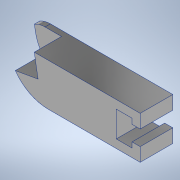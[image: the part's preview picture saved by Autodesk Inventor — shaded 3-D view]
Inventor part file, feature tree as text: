
AUTODESK INVENTOR PART (.ipt)
format: ipt  version: 2022 (Build 260153000, 153)  size: 164,352 bytes
history: native  units: mm
features: extrude x3, sketch x3, fillet x1
ambient origin geometry x8: Origin, YZ Plane, XZ Plane, XY Plane, X Axis, Y Axis, Z Axis, Center Point
bodies: Body1 (feature_tree)
feature tree (7):
  extrude  "Extrusion2"  Depth=5.8mm
  extrude  "Extrusion7"  Depth=12.0mm TaperAngle=0.0deg
  extrude  "Extrusion10"  Depth=15.6mm
  fillet  "Fillet2"  [1 undecoded]
  sketch  "Sketch5"  dims[d41=5.8mm d48=44.0mm]
  sketch  "Sketch11"  dims[d50=3.0mm d56=12.0mm d57=0.0mm]
  sketch  "Sketch14"  dims[d63=45.0mm d67=15.6mm d71=0.0mm d72=36.2mm d87=5.6mm d88=9.5mm d95=17.453293mm d96=8.0mm d97=15.0mm d98=10.0mm d99=0.0mm d107=10.0mm d108=0.0mm d109=0.0mm d110=15.0mm]
note: 1 required parameter value undecoded (feature->parameter linkage not recoverable at this tier; creation-order binding heuristic only, values carry confidence <= 0.55)
